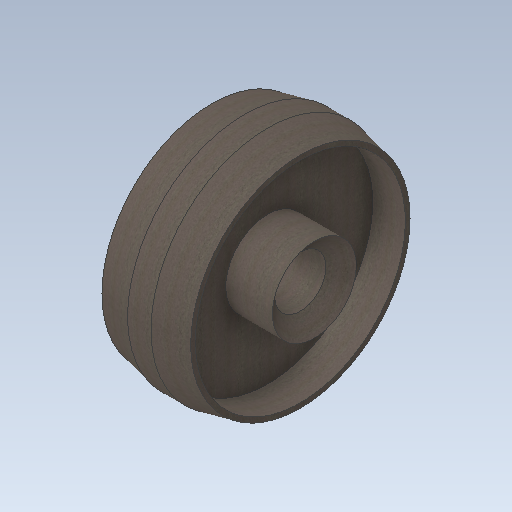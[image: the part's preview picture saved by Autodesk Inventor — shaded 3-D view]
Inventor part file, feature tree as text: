
AUTODESK INVENTOR PART (.ipt)
format: ipt  version: 2020 (Build 240168000, 168)  size: 246,272 bytes
history: native  units: mm
features: revolve x1, sketch x1
ambient origin geometry x8: Origin, YZ Plane, XZ Plane, XY Plane, X Axis, Y Axis, Z Axis, Center Point
bodies: Solid1 (feature_tree)
feature tree (2):
  revolve  "Revolution1"  [1 undecoded]
  sketch  "Sketch1"  dims[d0=50.0mm d1=18.0mm d2=38.0mm d3=11.0mm d4=39.0mm d5=27.0mm d8=10.0mm d9=20.0mm d10=90.0deg d11=34.0mm d12=2.0mm d13=2.0mm d14=18.0mm d15=26.248585mm d16=11.714245mm d17=18.0mm d18=45.0mm]
note: 1 required parameter value undecoded (feature->parameter linkage not recoverable at this tier; creation-order binding heuristic only, values carry confidence <= 0.55)
